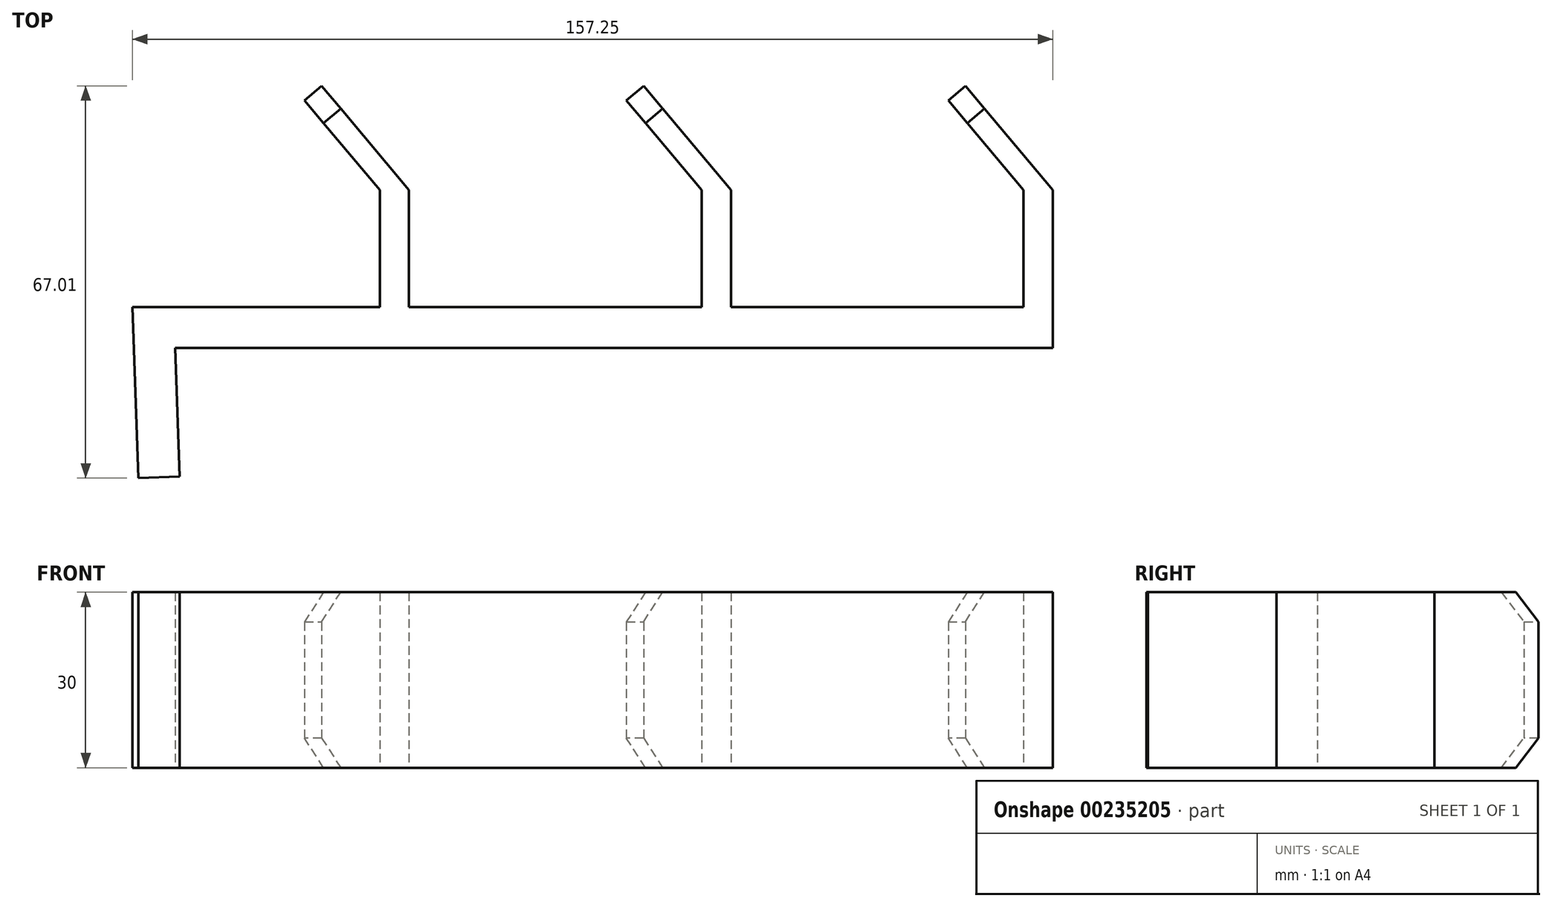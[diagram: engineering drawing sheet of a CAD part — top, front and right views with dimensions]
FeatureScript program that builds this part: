
annotation { "Feature Type Name" : "Feature", "Feature Type Description" : "" }
export const myFeature = defineFeature(function(context is Context, id is Id, definition is map)
    precondition{}
    {
        {
            var Q0;
            Q0=qCreatedBy(makeId("Top.planeOp"),FACE);
            var sketch = newSketch(context, id + "F0", { "sketchPlane" : qUnion([Q0])});
            skLineSegment(sketch, "E0", {"start": v(-48.9, -7) * mm, "end": v(101.1, -7) * mm});
            skLineSegment(sketch, "E1", {"start": v(101.1, -7) * mm, "end": v(101.1, 20) * mm});
            skLineSegment(sketch, "E2", {"start": v(101.1, 20) * mm, "end": v(86.17, 37.78) * mm});
            skLineSegment(sketch, "E3", {"start": v(86.17, 37.78) * mm, "end": v(83.24, 35.32) * mm});
            skLineSegment(sketch, "E4", {"start": v(83.24, 35.32) * mm, "end": v(96.1, 20) * mm});
            skLineSegment(sketch, "E5", {"start": v(96.1, 20) * mm, "end": v(96.1, 0) * mm});
            skLineSegment(sketch, "E6", {"start": v(96.1, 0) * mm, "end": v(46.1, 0) * mm});
            skLineSegment(sketch, "E7", {"start": v(46.1, 0) * mm, "end": v(46.1, 20) * mm});
            skLineSegment(sketch, "E8", {"start": v(46.1, 20) * mm, "end": v(31.17, 37.78) * mm});
            skLineSegment(sketch, "E9", {"start": v(31.17, 37.78) * mm, "end": v(28.23, 35.32) * mm});
            skLineSegment(sketch, "E10", {"start": v(28.23, 35.32) * mm, "end": v(41.1, 19.99) * mm});
            skLineSegment(sketch, "E11", {"start": v(41.1, 19.99) * mm, "end": v(41.1, 0) * mm});
            skLineSegment(sketch, "E12", {"start": v(41.1, 0) * mm, "end": v(-8.9, 0) * mm});
            skLineSegment(sketch, "E13", {"start": v(-8.9, 0) * mm, "end": v(-8.9, 19.99) * mm});
            skLineSegment(sketch, "E14", {"start": v(-8.9, 19.99) * mm, "end": v(-23.83, 37.78) * mm});
            skLineSegment(sketch, "E15", {"start": v(-23.83, 37.78) * mm, "end": v(-26.77, 35.32) * mm});
            skLineSegment(sketch, "E16", {"start": v(-26.77, 35.32) * mm, "end": v(-13.91, 19.99) * mm});
            skLineSegment(sketch, "E17", {"start": v(-13.91, 19.99) * mm, "end": v(-13.91, 0) * mm});
            skLineSegment(sketch, "E18", {"start": v(-48.9, -7) * mm, "end": v(-48.14, -28.99) * mm});
            skLineSegment(sketch, "E19", {"start": v(-55.13, -29.23) * mm, "end": v(-56.15, 0) * mm});
            skLineSegment(sketch, "E20", {"start": v(-55.13, -29.23) * mm, "end": v(-48.14, -28.99) * mm});
            skLineSegment(sketch, "E21", {"start": v(-56.15, 0) * mm, "end": v(-13.91, 0) * mm});
            skSolve(sketch);
        }
        {
            var Q0;
            Q0 = qSketchRegion(id + "F0", true);
            extrude(context, id + "F1", {"entities" : qUnion([Q0]), "depth" : 30 * mm});
        }
        {
            var Q0;
            Q0=makeQuery(id+"F1.opExtrude","CAP_EDGE",EDGE,{"disambiguationData":[OSD([sQuery(id+"F0.wireOp",EDGE,"E15")])],"isStart":false});
            var Q1;
            Q1=makeQuery(id+"F1.opExtrude","CAP_EDGE",EDGE,{"disambiguationData":[OSD([sQuery(id+"F0.wireOp",EDGE,"E15")])],"isStart":true});
            var Q2;
            Q2=makeQuery(id+"F1.opExtrude","CAP_EDGE",EDGE,{"disambiguationData":[OSD([sQuery(id+"F0.wireOp",EDGE,"E9")])],"isStart":true});
            var Q3;
            Q3=makeQuery(id+"F1.opExtrude","CAP_EDGE",EDGE,{"disambiguationData":[OSD([sQuery(id+"F0.wireOp",EDGE,"E9")])],"isStart":false});
            var Q4;
            Q4=makeQuery(id+"F1.opExtrude","CAP_EDGE",EDGE,{"disambiguationData":[OSD([sQuery(id+"F0.wireOp",EDGE,"E3")])],"isStart":false});
            var Q5;
            Q5=makeQuery(id+"F1.opExtrude","CAP_EDGE",EDGE,{"disambiguationData":[OSD([sQuery(id+"F0.wireOp",EDGE,"E3")])],"isStart":true});
            chamfer(context, id + "F2", {"entities" : qUnion([Q0, Q1, Q2, Q3, Q4, Q5]), "chamferType" : ChamferType.OFFSET_ANGLE, "width" : 5.08 * mm, "oppositeDirection" : false, "angle" : 45 * degree, "tangentPropagation" : true});
        }
    });
